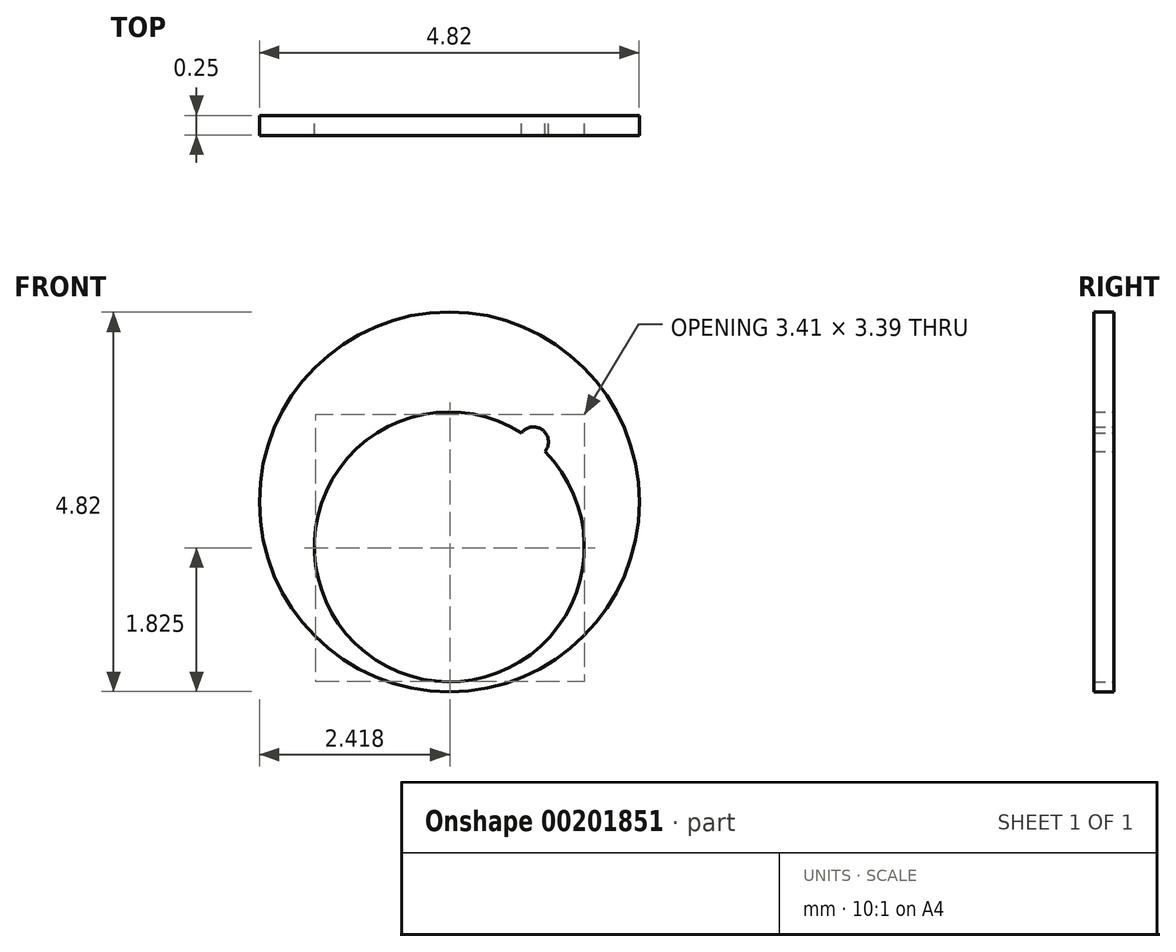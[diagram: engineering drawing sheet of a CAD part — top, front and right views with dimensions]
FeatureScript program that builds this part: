
annotation { "Feature Type Name" : "Feature", "Feature Type Description" : "" }
export const myFeature = defineFeature(function(context is Context, id is Id, definition is map)
    precondition{}
    {
        {
            var Q0;
            Q0=qCreatedBy(makeId("Front.planeOp"),FACE);
            var sketch = newSketch(context, id + "F0", { "sketchPlane" : qUnion([Q0])});
            skCircle(sketch, "E0", {"center": v(0, -0.57) * mm, "radius": 1.59 * mm});
            skCircle(sketch, "E1", {"center": v(0, 0) * mm, "radius": 0.89 * mm});
            skCircle(sketch, "E2", {"center": v(0, -1.52) * mm, "radius": 0.5 * mm});
            skCircle(sketch, "E3", {"center": v(0, -0.57) * mm, "radius": 1.71 * mm});
            skCircle(sketch, "E4", {"center": v(0, 0) * mm, "radius": 2.41 * mm});
            skCircle(sketch, "E5", {"center": v(0.32, 0.76) * mm, "radius": 0.2 * mm});
            skCircle(sketch, "E6", {"center": v(1.07, 0.76) * mm, "radius": 0.2 * mm});
            skSolve(sketch);
        }
        {
            var Q0;
            Q0 = qSketchRegion(id + "F0", true);
            extrude(context, id + "F1", {"entities" : qUnion([Q0]), "depth" : 0.25 * mm});
        }
    });
